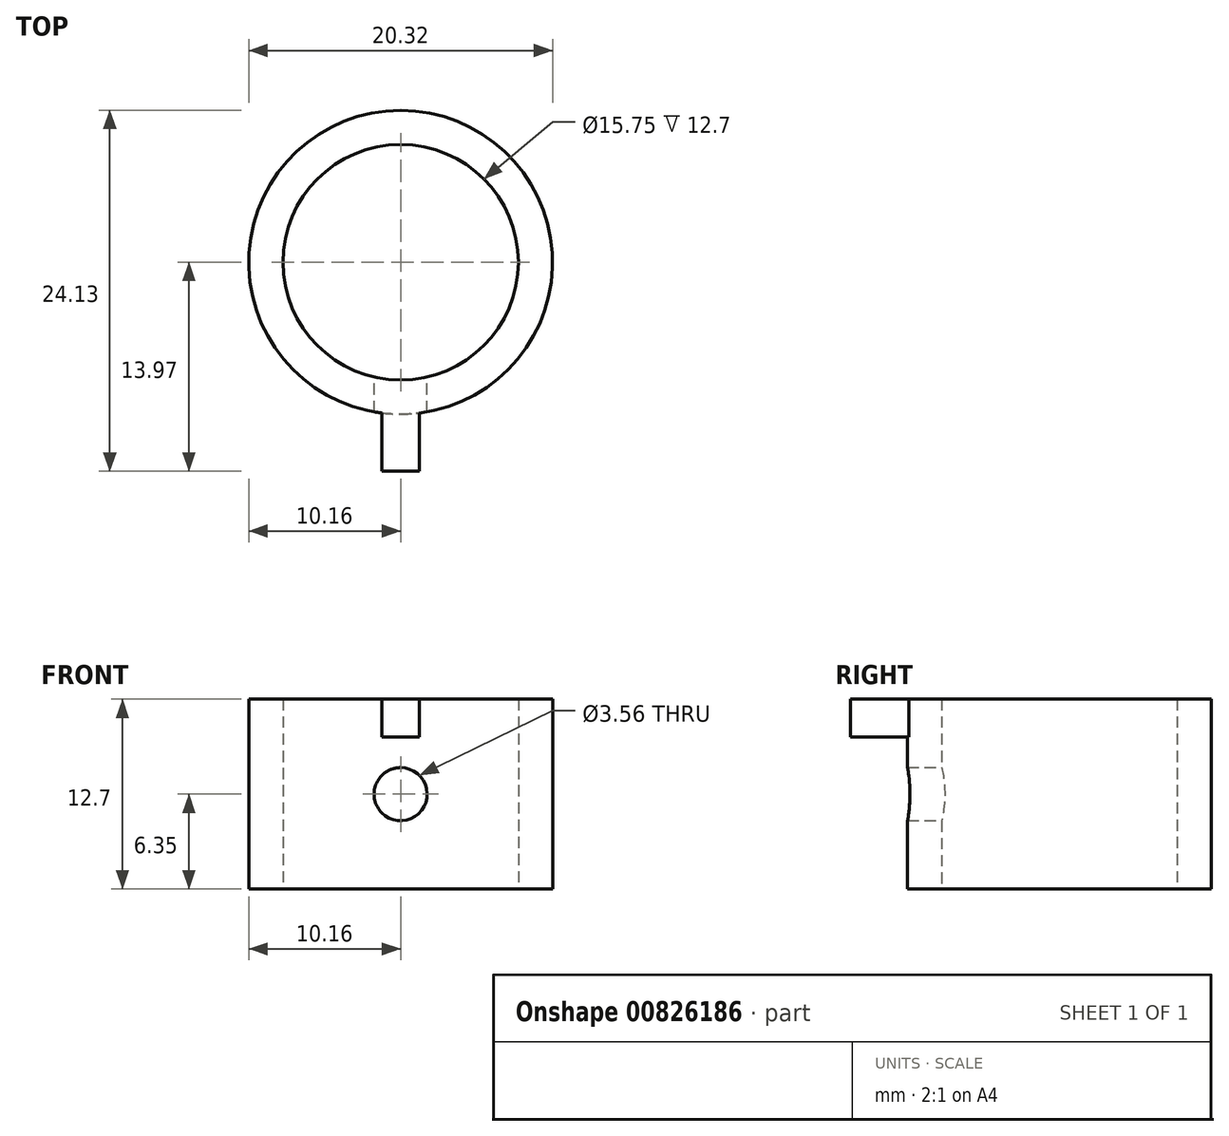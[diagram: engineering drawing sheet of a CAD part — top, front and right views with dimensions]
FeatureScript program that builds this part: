
annotation { "Feature Type Name" : "Feature", "Feature Type Description" : "" }
export const myFeature = defineFeature(function(context is Context, id is Id, definition is map)
    precondition{}
    {
        {
            var Q0;
            Q0=qCreatedBy(makeId("Top.planeOp"),FACE);
            var sketch = newSketch(context, id + "F0", { "sketchPlane" : qUnion([Q0])});
            skCircle(sketch, "E0", {"center": v(0, 0) * mm, "radius": 10.16 * mm});
            skSolve(sketch);
        }
        {
            var Q0;
            Q0=makeQuery(id+"F0.imprint","IMPRINT",FACE,{"disambiguationData":[TD([[makeQuery(id+"F0.imprint","IMPRINT",EDGE,{"derivedFrom":sQuery(id+"F0.wireOp",EDGE,"E0")}),1.0]])]});
            extrude(context, id + "F1", {"entities" : qUnion([Q0]), "depth" : 12.7 * mm, "offsetDistance" : 25.4 * mm});
        }
        {
            var Q0;
            Q0=qCreatedBy(makeId("Front.planeOp"),FACE);
            var sketch = newSketch(context, id + "F2", { "sketchPlane" : qUnion([Q0])});
            skLineSegment(sketch, "E1", {"start": v(0, 0) * mm, "end": v(0, 11.43) * mm});
            skLineSegment(sketch, "E2.bottom", {"start": v(-1.27, 10.16) * mm, "end": v(1.27, 10.16) * mm});
            skLineSegment(sketch, "E2.top", {"start": v(-1.27, 12.7) * mm, "end": v(1.27, 12.7) * mm});
            skLineSegment(sketch, "E2.left", {"start": v(-1.27, 10.16) * mm, "end": v(-1.27, 12.7) * mm});
            skLineSegment(sketch, "E2.right", {"start": v(1.27, 10.16) * mm, "end": v(1.27, 12.7) * mm});
            skPoint(sketch, "E2.middle", {"position": v(0, 11.43) * mm});
            skSolve(sketch);
        }
        {
            var Q0;
            Q0 = qSketchRegion(id + "F2", true);
            extrude(context, id + "F3", {"entities" : qUnion([Q0]), "operationType" : NewBodyOperationType.ADD, "depth" : 13.97 * mm, "offsetDistance" : 25.4 * mm});
        }
        {
            var Q0;
            Q0=qCreatedBy(makeId("Front.planeOp"),FACE);
            var sketch = newSketch(context, id + "F4", { "sketchPlane" : qUnion([Q0])});
            skLineSegment(sketch, "E3", {"start": v(0, 0) * mm, "end": v(0, 6.35) * mm});
            skCircle(sketch, "E4", {"center": v(0, 6.35) * mm, "radius": 1.78 * mm});
            skSolve(sketch);
        }
        {
            var Q0;
            Q0=makeQuery(id+"F4.imprint","IMPRINT",FACE,{"disambiguationData":[TD([[makeQuery(id+"F4.imprint","IMPRINT",EDGE,{"derivedFrom":sQuery(id+"F4.wireOp",EDGE,"E4")}),1.0]])]});
            extrude(context, id + "F5", {"entities" : qUnion([Q0]), "operationType" : NewBodyOperationType.REMOVE, "endBound" : BoundingType.UP_TO_NEXT, "depth" : 25.4 * mm, "offsetDistance" : 25.4 * mm});
        }
        {
            var Q0;
            Q0=makeQuery(id+"F1.opExtrude","CAP_FACE",FACE,{"disambiguationData":[OSD([sQuery(id+"F0.wireOp",EDGE,"E0")])],"isStart":true});
            var sketch = newSketch(context, id + "F6", { "sketchPlane" : qUnion([Q0])});
            skPoint(sketch, "E5", {"position": v(0, 0) * mm});
            skSolve(sketch);
        }
        {
            var Q0;
            Q0=sQuery(id+"F6.wireOp",VERTEX,"E5");
            var Q1;
            Q1=makeQuery(id+"F1.opExtrude","SWEPT_BODY",BODY,{"disambiguationData":[OSD([sQuery(id+"F0.wireOp",EDGE,"E0")])]});
            hole(context, id + "F7", {"style" : HoleStyle.SIMPLE, "endStyle" : HoleEndStyle.THROUGH, "holeDiameter" : 15.75 * mm, "majorDiameter" : 6.35 * mm, "isTappedThrough" : true, "tappedDepth" : 12.7 * mm, "tapClearance" : 3, "locations" : qUnion([Q0]), "scope" : qUnion([Q1])});
        }
    });
